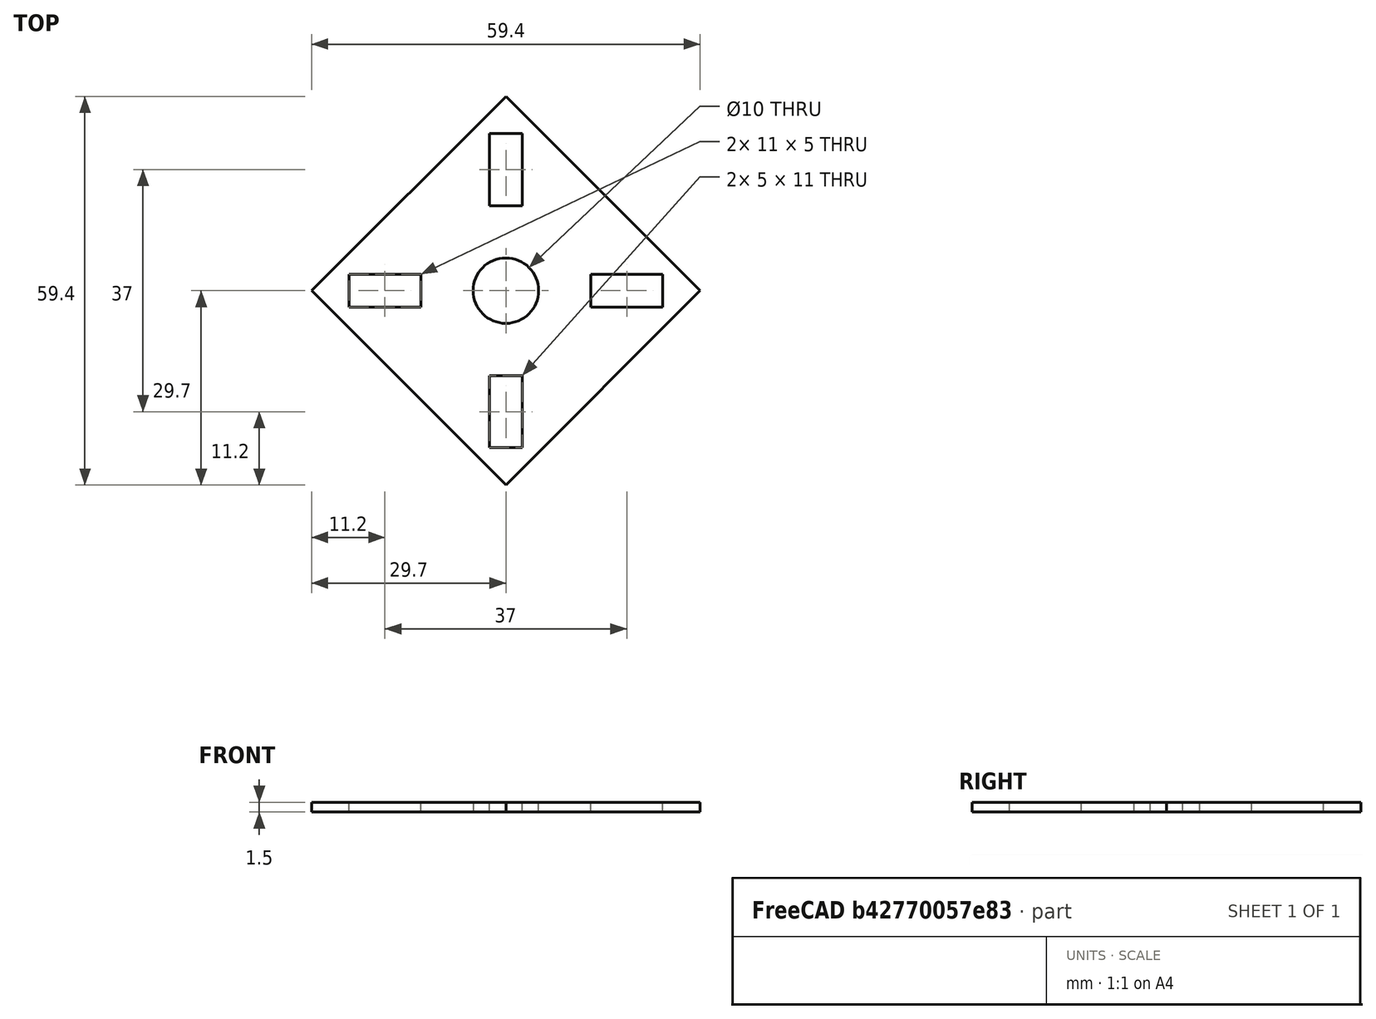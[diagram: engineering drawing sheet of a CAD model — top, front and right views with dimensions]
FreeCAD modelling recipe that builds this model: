
FCSTD DOCUMENT  (FreeCAD 0.14R3702 (Git))
Label: tapa_rodamiento
License: CC-BY 3.0
LicenseURL: http://creativecommons.org/licenses/by/3.0/
objects: Sketcher::SketchObject×1, PartDesign::Pad×1
note: 3 computed .brp shape members not serialized (recipe doc carries the construction recipe); baked Part::Feature solids carry a one-line shape summary decoded from their .brp

FEATURE [Sketcher::SketchObject] Sketch  label="Tapa"
  sketch-geometry (21):
    g0: Circle CenterX=0 CenterY=0 CenterZ=0 NormalX=0 NormalY=0 NormalZ=1 Radius=5
    g1: LineSegment StartX=-24 StartY=2.5 StartZ=0 EndX=-13 EndY=2.5 EndZ=0
    g2: LineSegment StartX=-13 StartY=2.5 StartZ=0 EndX=-13 EndY=-2.5 EndZ=0
    g3: LineSegment StartX=-13 StartY=-2.5 StartZ=0 EndX=-24 EndY=-2.5 EndZ=0
    g4: LineSegment StartX=-24 StartY=-2.5 StartZ=0 EndX=-24 EndY=2.5 EndZ=0
    g5: LineSegment StartX=-2.5 StartY=24 StartZ=0 EndX=2.5 EndY=24 EndZ=0
    g6: LineSegment StartX=2.5 StartY=24 StartZ=0 EndX=2.5 EndY=13 EndZ=0
    g7: LineSegment StartX=2.5 StartY=13 StartZ=0 EndX=-2.5 EndY=13 EndZ=0
    g8: LineSegment StartX=-2.5 StartY=13 StartZ=0 EndX=-2.5 EndY=24 EndZ=0
    g9: LineSegment StartX=-2.5 StartY=-13 StartZ=0 EndX=2.5 EndY=-13 EndZ=0
    g10: LineSegment StartX=2.5 StartY=-13 StartZ=0 EndX=2.5 EndY=-24 EndZ=0
    g11: LineSegment StartX=2.5 StartY=-24 StartZ=0 EndX=-2.5 EndY=-24 EndZ=0
    g12: LineSegment StartX=-2.5 StartY=-24 StartZ=0 EndX=-2.5 EndY=-13 EndZ=0
    g13: LineSegment StartX=13 StartY=2.5 StartZ=0 EndX=24 EndY=2.5 EndZ=0
    g14: LineSegment StartX=24 StartY=2.5 StartZ=0 EndX=24 EndY=-2.5 EndZ=0
    g15: LineSegment StartX=24 StartY=-2.5 StartZ=0 EndX=13 EndY=-2.5 EndZ=0
    g16: LineSegment StartX=13 StartY=-2.5 StartZ=0 EndX=13 EndY=2.5 EndZ=0
    g17: LineSegment StartX=29.6985 StartY=0 StartZ=0 EndX=0 EndY=29.6985 EndZ=0
    g18: LineSegment StartX=0 StartY=29.6985 StartZ=0 EndX=-29.6985 EndY=0 EndZ=0
    g19: LineSegment StartX=-29.6985 StartY=0 StartZ=0 EndX=0 EndY=-29.6985 EndZ=0
    g20: LineSegment StartX=0 StartY=-29.6985 StartZ=0 EndX=29.6985 EndY=0 EndZ=0
  constraints (62):
    c: Radius(g0) = 5
    c: Coincident(g1,g2)
    c: Coincident(g2,g3)
    c: Coincident(g3,g4)
    c: Coincident(g4,g1)
    c: Horizontal(g1)
    c: Horizontal(g3)
    c: Vertical(g2)
    c: Vertical(g4)
    c: Coincident(g5,g6)
    c: Coincident(g6,g7)
    c: Coincident(g7,g8)
    c: Coincident(g8,g5)
    c: Horizontal(g5)
    c: Horizontal(g7)
    c: Vertical(g6)
    c: Vertical(g8)
    c: Coincident(g9,g10)
    c: Coincident(g10,g11)
    c: Coincident(g11,g12)
    c: Coincident(g12,g9)
    c: Horizontal(g9)
    c: Horizontal(g11)
    c: Vertical(g10)
    c: Vertical(g12)
    c: Coincident(g13,g14)
    c: Coincident(g14,g15)
    c: Coincident(g15,g16)
    c: Coincident(g16,g13)
    c: Horizontal(g13)
    c: Horizontal(g15)
    c: Vertical(g14)
    c: Vertical(g16)
    c: Distance(g4) = 5
    c: Distance(g11) = 5
    c: Distance(g5) = 5
    c: Distance(g14) = 5
    c: Distance(g3) = 11
    c: Distance(g15) = 11
    c: Distance(g12) = 11
    c: Distance(g8) = 11
    c: DistanceY(g-1,g1) = 2.5
    c: DistanceY(g-1,g13) = 2.5
    c: DistanceX(g-1,g6) = 2.5
    c: DistanceX(g-1,g10) = 2.5
    c: DistanceX(g-1,g2) = -13
    c: DistanceX(g-1,g15) = 13
    c: DistanceY(g-1,g6) = 13
    c: DistanceY(g-1,g9) = -13
    c: Coincident(g0,g-1)
    c: Coincident(g17,g18)
    c: Coincident(g18,g19)
    c: Coincident(g19,g20)
    c: Coincident(g20,g17)
    c: Distance(g17) = 42
    c: Distance(g18) = 42
    c: Equal(g19,g17)
    c: Equal(g20,g18)
    c: DistanceX(g-1,g17) = 0
    c: DistanceX(g-1,g19) = 0
    c: DistanceY(g-1,g17) = 0
    c: Angle(g17,g-1) = 0.785398
FEATURE [PartDesign::Pad] Pad
  Length = 1.5
  Length2 = 100
  Sketch = -> Sketch
  Type = 0
